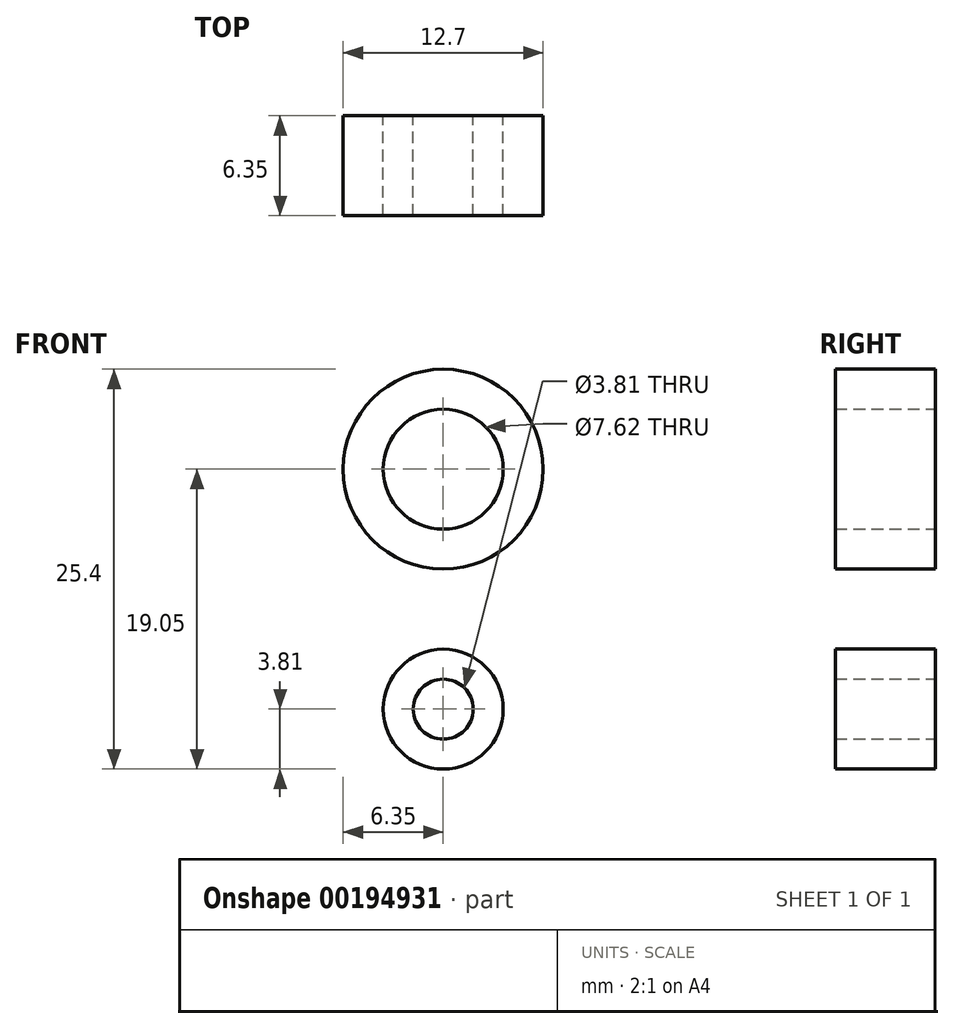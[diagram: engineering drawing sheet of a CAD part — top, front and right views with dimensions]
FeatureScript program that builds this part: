
annotation { "Feature Type Name" : "Feature", "Feature Type Description" : "" }
export const myFeature = defineFeature(function(context is Context, id is Id, definition is map)
    precondition{}
    {
        {
            var Q0;
            Q0=qCreatedBy(makeId("Front.planeOp"),FACE);
            var sketch = newSketch(context, id + "F0", { "sketchPlane" : qUnion([Q0])});
            skCircle(sketch, "E0", {"center": v(0, -8.9) * mm, "radius": 3.81 * mm});
            skCircle(sketch, "E1", {"center": v(0, -8.9) * mm, "radius": 1.9 * mm});
            skLineSegment(sketch, "E2", {"start": v(0, -5.08) * mm, "end": v(-2.54, -5.08) * mm});
            skLineSegment(sketch, "E3", {"start": v(-2.54, -5.08) * mm, "end": v(0, -5.08) * mm});
            skLineSegment(sketch, "E4", {"start": v(0, -5.08) * mm, "end": v(2.54, -5.08) * mm});
            skLineSegment(sketch, "E5", {"start": v(-2.54, -5.08) * mm, "end": v(-2.54, 0) * mm});
            skLineSegment(sketch, "E6", {"start": v(2.54, -5.08) * mm, "end": v(2.54, 0) * mm});
            skLineSegment(sketch, "E7", {"start": v(2.54, 0) * mm, "end": v(-2.54, 0) * mm});
            skLineSegment(sketch, "E8", {"start": v(0, 0) * mm, "end": v(2.54, 0) * mm});
            skLineSegment(sketch, "E9", {"start": v(-2.54, 0) * mm, "end": v(2.54, 0) * mm});
            skPoint(sketch, "E10.endSnap0", {"position": v(0, 12.7) * mm});
            skCircle(sketch, "E11", {"center": v(0, 6.35) * mm, "radius": 6.35 * mm});
            skCircle(sketch, "E12", {"center": v(0, 6.35) * mm, "radius": 3.81 * mm});
            skSolve(sketch);
        }
        {
            var Q0;
            Q0=makeQuery(id+"F0.imprint","IMPRINT",FACE,{"disambiguationData":[TD([[makeQuery(id+"F0.imprint","IMPRINT",EDGE,{"derivedFrom":sQuery(id+"F0.wireOp",EDGE,"E0")}),1.0]])]});
            var Q1;
            Q1=makeQuery(id+"F0.imprint","IMPRINT",FACE,{"disambiguationData":[TD([[makeQuery(id+"F0.imprint","IMPRINT",EDGE,{"derivedFrom":sQuery(id+"F0.wireOp",EDGE,"E3")}),1.0]])]});
            var Q2;
            Q2=makeQuery(id+"F0.imprint","IMPRINT",FACE,{"disambiguationData":[TD([[makeQuery(id+"F0.imprint","IMPRINT",EDGE,{"derivedFrom":sQuery(id+"F0.wireOp",EDGE,"E11")}),1.0]])]});
            extrude(context, id + "F1", {"entities" : qUnion([Q0, Q1, Q2]), "depth" : 6.35 * mm});
        }
    });
